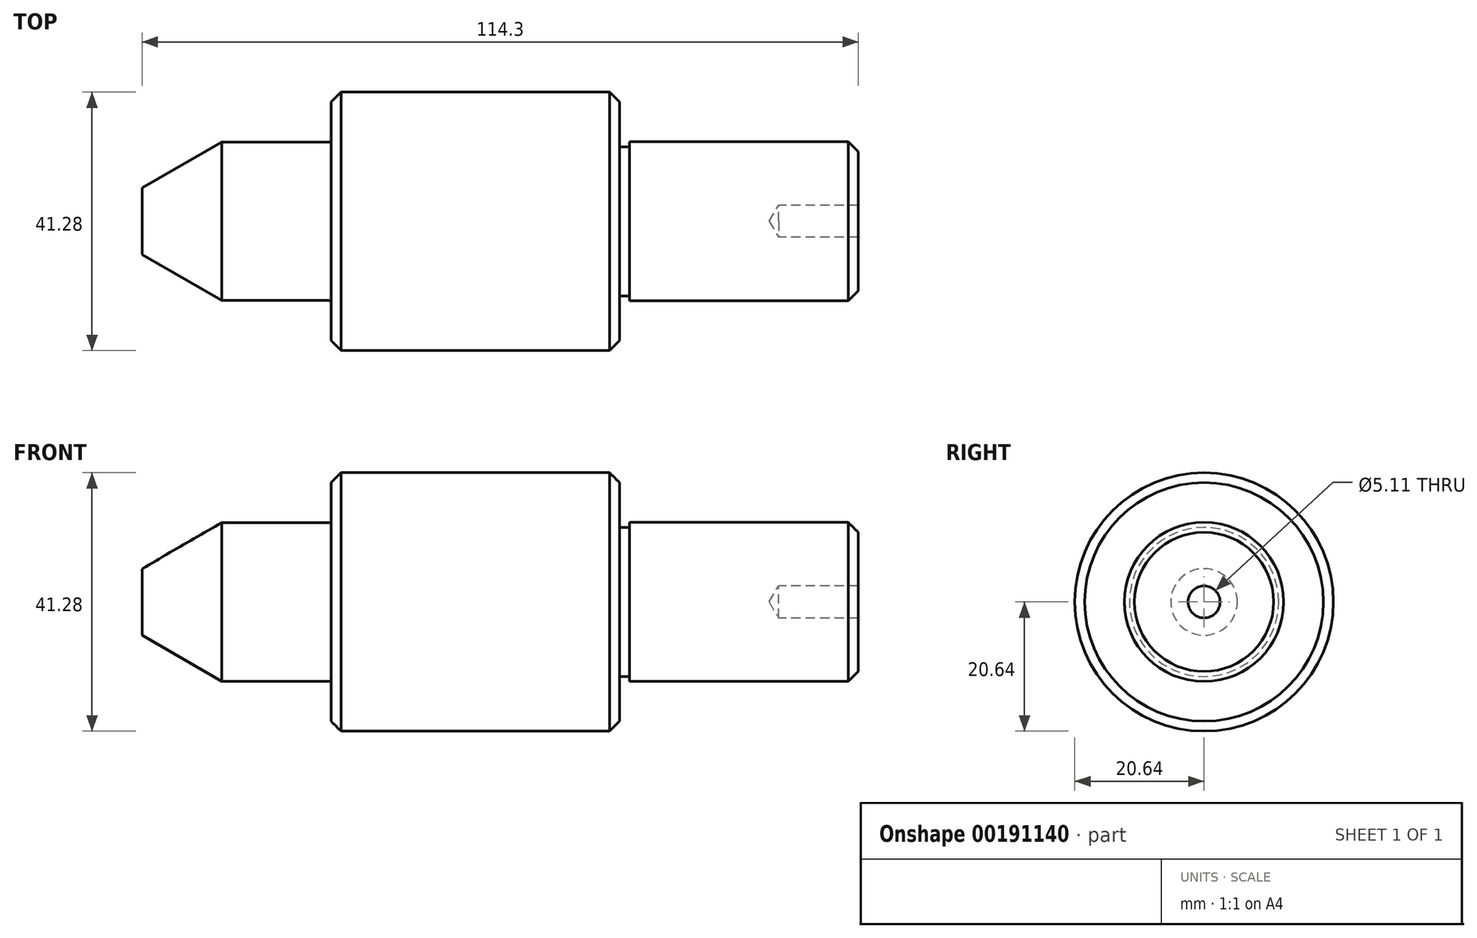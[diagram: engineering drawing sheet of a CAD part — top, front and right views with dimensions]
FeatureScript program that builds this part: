
annotation { "Feature Type Name" : "Feature", "Feature Type Description" : "" }
export const myFeature = defineFeature(function(context is Context, id is Id, definition is map)
    precondition{}
    {
        {
            var Q0;
            Q0=qCreatedBy(makeId("Front.planeOp"),FACE);
            var sketch = newSketch(context, id + "F0", { "sketchPlane" : qUnion([Q0])});
            skLineSegment(sketch, "E0", {"start": v(0, 0) * mm, "end": v(0, 12.7) * mm});
            skLineSegment(sketch, "E1", {"start": v(-38.1, 12.7) * mm, "end": v(-38.1, 20.64) * mm});
            skLineSegment(sketch, "E2", {"start": v(-38.1, 20.64) * mm, "end": v(-84.14, 20.64) * mm});
            skLineSegment(sketch, "E3", {"start": v(-84.14, 20.64) * mm, "end": v(-84.14, 12.65) * mm});
            skLineSegment(sketch, "E4", {"start": v(-84.14, 12.65) * mm, "end": v(-101.6, 12.65) * mm});
            skLineSegment(sketch, "E5", {"start": v(-101.6, 12.65) * mm, "end": v(-114.3, 5.32) * mm});
            skLineSegment(sketch, "E6", {"start": v(-114.3, 5.32) * mm, "end": v(-114.3, 0) * mm});
            skLineSegment(sketch, "E7", {"start": v(-114.3, 0) * mm, "end": v(0, 0) * mm});
            skLineSegment(sketch, "E8", {"start": v(0, 12.7) * mm, "end": v(-38.1, 12.7) * mm});
            skSolve(sketch);
        }
        {
            var Q0;
            Q0 = qSketchRegion(id + "F0", true);
            var Q1;
            Q1=sQuery(id+"F0.wireOp",EDGE,"E7");
            revolve(context, id + "F1", {"entities" : qUnion([Q0]), "axis" : qUnion([Q1]), "revolveType" : RevolveType.FULL});
        }
        {
            var Q0;
            Q0=qCreatedBy(makeId("Top.planeOp"),FACE);
            var sketch = newSketch(context, id + "F2", { "sketchPlane" : qUnion([Q0])});
            skLineSegment(sketch, "E9.bottom", {"start": v(-38.1, -12.7) * mm, "end": v(-36.51, -12.7) * mm});
            skLineSegment(sketch, "E9.top", {"start": v(-38.1, -11.9) * mm, "end": v(-36.51, -11.9) * mm});
            skLineSegment(sketch, "E9.left", {"start": v(-38.1, -12.7) * mm, "end": v(-38.1, -11.9) * mm});
            skLineSegment(sketch, "E9.right", {"start": v(-36.51, -12.7) * mm, "end": v(-36.51, -11.9) * mm});
            skLineSegment(sketch, "E10", {"start": v(0, -12.7) * mm, "end": v(-31.75, -12.7) * mm});
            skLineSegment(sketch, "E11", {"start": v(0, -12.7) * mm, "end": v(-31.75, -12.7) * mm, "construction": true});
            skLineSegment(sketch, "E12", {"start": v(0, 0) * mm, "end": v(-130.08, 0) * mm, "construction": true});
            skSolve(sketch);
        }
        {
            var Q0;
            Q0 = qSketchRegion(id + "F2", true);
            var Q1;
            Q1=sQuery(id+"F2.wireOp",EDGE,"E12");
            revolve(context, id + "F3", {"operationType" : NewBodyOperationType.REMOVE, "entities" : qUnion([Q0]), "axis" : qUnion([Q1]), "revolveType" : RevolveType.FULL, "oppositeDirection" : true});
        }
        {
            var Q0;
            Q0=makeQuery(id+"F1.opRevolve","SWEPT_EDGE",EDGE,{"disambiguationData":[OSD([sQuery(id+"F0.wireOp",EDGE,"E0"),sQuery(id+"F0.wireOp",EDGE,"E8")])]});
            var Q1;
            Q1=makeQuery(id+"F1.opRevolve","SWEPT_EDGE",EDGE,{"disambiguationData":[OSD([sQuery(id+"F0.wireOp",EDGE,"E1"),sQuery(id+"F0.wireOp",EDGE,"E2")])]});
            var Q2;
            Q2=makeQuery(id+"F1.opRevolve","SWEPT_EDGE",EDGE,{"disambiguationData":[OSD([sQuery(id+"F0.wireOp",EDGE,"E2"),sQuery(id+"F0.wireOp",EDGE,"E3")])]});
            chamfer(context, id + "F4", {"entities" : qUnion([Q0, Q1, Q2]), "width" : 1.59 * mm, "tangentPropagation" : true});
        }
        {
            var Q0;
            Q0=makeQuery(id+"F1.opRevolve","SWEPT_EDGE",EDGE,{"disambiguationData":[OSD([sQuery(id+"F0.wireOp",EDGE,"E3"),sQuery(id+"F0.wireOp",EDGE,"E4")])]});
            fillet(context, id + "F5", {"entities" : qUnion([Q0]), "radius" : 0.38 * mm, "tangentPropagation" : true, "allowEdgeOverflow" : false});
        }
        {
            var Q0;
            Q0=makeQuery(id+"F1.opRevolve","SWEPT_FACE",FACE,{"disambiguationData":[OSD([sQuery(id+"F0.wireOp",EDGE,"E0")])]});
            var sketch = newSketch(context, id + "F6", { "sketchPlane" : qUnion([Q0])});
            skPoint(sketch, "E13", {"position": v(0, 0) * mm});
            skSolve(sketch);
        }
        {
            var Q0;
            Q0=sQuery(id+"F6.wireOp",VERTEX,"E13");
            var Q1;
            Q1=makeQuery(id+"F1.opRevolve","SWEPT_BODY",BODY,{"disambiguationData":[OSD([sQuery(id+"F0.wireOp",EDGE,"E0"),sQuery(id+"F0.wireOp",EDGE,"E1"),sQuery(id+"F0.wireOp",EDGE,"E2"),sQuery(id+"F0.wireOp",EDGE,"E3"),sQuery(id+"F0.wireOp",EDGE,"E4"),sQuery(id+"F0.wireOp",EDGE,"E5"),sQuery(id+"F0.wireOp",EDGE,"E6"),sQuery(id+"F0.wireOp",EDGE,"E7"),sQuery(id+"F0.wireOp",EDGE,"E8")])]});
            hole(context, id + "F7", {"style" : HoleStyle.SIMPLE, "endStyle" : HoleEndStyle.BLIND, "standardTappedOrClearance" : lookupTablePath({ "standard" : "ANSI", "engagement" : "75%", "pitch" : "20 tpi", "size" : "1/4", "type" : "Tapped" }), "standardBlindInLast" : lookupTablePath({ "standard" : "ANSI", "engagement" : "75%", "pitch" : "20 tpi", "size" : "1/4", "type" : "Tapped" }), "holeDiameter" : 5.1 * mm, "holeDepth" : 12.7 * mm, "startFromSketch" : true, "locations" : qUnion([Q0]), "scope" : qUnion([Q1]), "majorDiameter" : 6.35 * mm});
        }
    });
